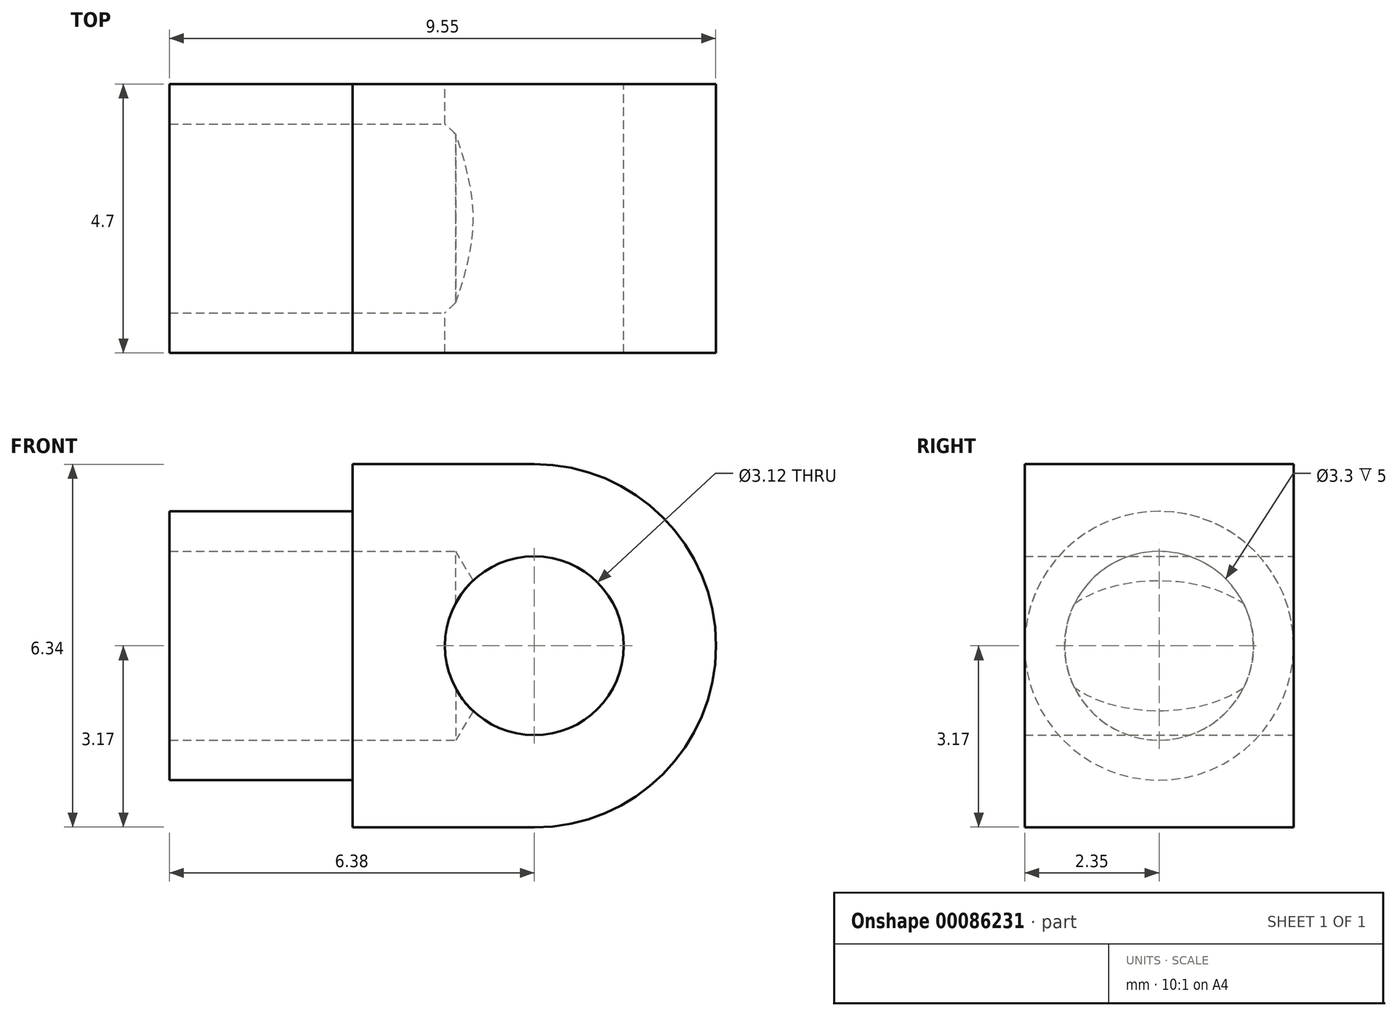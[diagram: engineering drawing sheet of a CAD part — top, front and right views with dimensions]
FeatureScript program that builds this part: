
annotation { "Feature Type Name" : "Feature", "Feature Type Description" : "" }
export const myFeature = defineFeature(function(context is Context, id is Id, definition is map)
    precondition{}
    {
        {
            var Q0;
            Q0=qCreatedBy(makeId("Front.planeOp"),FACE);
            var sketch = newSketch(context, id + "F0", { "sketchPlane" : qUnion([Q0])});
            skLineSegment(sketch, "E0.bottom", {"start": v(-3.17, 3.17) * mm, "end": v(0, 3.17) * mm});
            skLineSegment(sketch, "E0.top", {"start": v(-3.17, -3.17) * mm, "end": v(0, -3.17) * mm});
            skLineSegment(sketch, "E0.left", {"start": v(-3.17, 3.17) * mm, "end": v(-3.17, -3.17) * mm});
            skArc(sketch, "E1", {"start": v(0, -3.17) * mm, "mid": v(3.17, 0) * mm, "end": v(0, 3.17) * mm});
            skPoint(sketch, "E2", {"position": v(3.17, 0) * mm});
            skCircle(sketch, "E3", {"center": v(0, 0) * mm, "radius": 1.56 * mm});
            skSolve(sketch);
        }
        {
            var Q0;
            Q0=makeQuery(id+"F0.imprint","IMPRINT",FACE,{"disambiguationData":[TD([[makeQuery(id+"F0.imprint","IMPRINT",EDGE,{"derivedFrom":sQuery(id+"F0.wireOp",EDGE,"E0.bottom")}),-1.0]])]});
            extrude(context, id + "F1", {"entities" : qUnion([Q0]), "depth" : 4.7 * mm, "offsetDistance" : 25 * mm, "symmetric" : true});
        }
        {
            var Q0;
            Q0=makeQuery(id+"F1.opExtrude","SWEPT_FACE",FACE,{"disambiguationData":[OSD([sQuery(id+"F0.wireOp",EDGE,"E0.left")])]});
            var sketch = newSketch(context, id + "F2", { "sketchPlane" : qUnion([Q0])});
            skCircle(sketch, "E4", {"center": v(0, 0) * mm, "radius": 2.35 * mm});
            skSolve(sketch);
        }
        {
            var Q0;
            {var subQ0=sQuery(id+"F2.wireOp",EDGE,"E4");var subQ1=sQuery(id+"F0.wireOp",EDGE,"E0.left");var subQ2=makeQuery(id+"F2.imprint","INTERSECT",VERTEX,{"derivedFrom":[makeQuery(id+"F1.opExtrude","CAP_EDGE",EDGE,{"disambiguationData":[OSD([subQ1])],"isStart":true}),subQ0]});Q0=makeQuery(id+"F2.imprint","IMPRINT",FACE,{"disambiguationData":[TD([[makeQuery(id+"F2.imprint","IMPRINT",EDGE,{"disambiguationData":[TD([[subQ2,1.0]])],"derivedFrom":subQ0}),1.0]])]});}
            extrude(context, id + "F3", {"entities" : qUnion([Q0]), "operationType" : NewBodyOperationType.ADD, "depth" : 3.2 * mm, "offsetDistance" : 25 * mm});
        }
        {
            var Q0;
            Q0=makeQuery(id+"F3.opExtrude","CAP_FACE",FACE,{"disambiguationData":[OSD([sQuery(id+"F2.wireOp",EDGE,"E4")])],"isStart":false});
            var sketch = newSketch(context, id + "F4", { "sketchPlane" : qUnion([Q0])});
            skPoint(sketch, "E5", {"position": v(0, 0) * mm});
            skSolve(sketch);
        }
        {
            var Q0;
            Q0=sQuery(id+"F4.wireOp",VERTEX,"E5");
            var Q1;
            Q1=makeQuery(id+"F1.opExtrude","SWEPT_BODY",BODY,{"disambiguationData":[OSD([sQuery(id+"F0.wireOp",EDGE,"E0.bottom"),sQuery(id+"F0.wireOp",EDGE,"E0.top"),sQuery(id+"F0.wireOp",EDGE,"E0.left"),sQuery(id+"F0.wireOp",EDGE,"E1"),sQuery(id+"F0.wireOp",EDGE,"E3")])]});
            hole(context, id + "F5", {"style" : HoleStyle.SIMPLE, "endStyle" : HoleEndStyle.BLIND, "standardTappedOrClearance" : lookupTablePath({ "fit" : "Normal", "standard" : "ISO", "size" : "M3", "type" : "Clearance" }), "standardBlindInLast" : lookupTablePath({ "fit" : "Standard", "standard" : "ISO", "size" : "M3", "type" : "Clearance" }), "holeDiameter" : 3.3 * mm, "majorDiameter" : 5 * mm, "holeDepth" : 5 * mm, "isTappedThrough" : true, "tappedDepth" : 3.47 * mm, "tapClearance" : 1, "locations" : qUnion([Q0]), "scope" : qUnion([Q1])});
        }
    });
